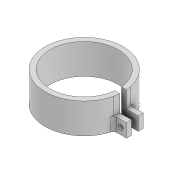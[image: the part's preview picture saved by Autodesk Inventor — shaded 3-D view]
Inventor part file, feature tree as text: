
AUTODESK INVENTOR PART (.ipt)
format: ipt  version: 2022 (Build 260153000, 153)  size: 139,264 bytes
history: native  units: mm
features: extrude x3, sketch x3, fillet x1, projected_geometry x1
ambient origin geometry x8: Origin, YZ Plane, XZ Plane, XY Plane, X Axis, Y Axis, Z Axis, Center Point
bodies: Solid1 (feature_tree)
feature tree (8):
  extrude  "Extrusion1"  Depth=3.0mm
  extrude  "Extrusion2"  Depth=2.0mm
  extrude  "Extrusion3"  Depth=18.0mm TaperAngle=0.0deg
  fillet  "Fillet1"  Radius=10.0mm
  sketch  "Sketch1"  dims[d0=40.5mm d2=3.0mm]
  sketch  "Sketch2"  dims[d3=3.0mm d4=2.0mm]
  projected_geometry  "Projected Loop1"
  sketch  "Sketch3"  dims[d5=10.0mm d6=18.0mm d7=0.0mm d8=10.0mm d9=0.0mm d11=3.2mm d12=4.0mm d14=22.0mm d15=0.0mm d16=2.0mm d17=3.0mm]
